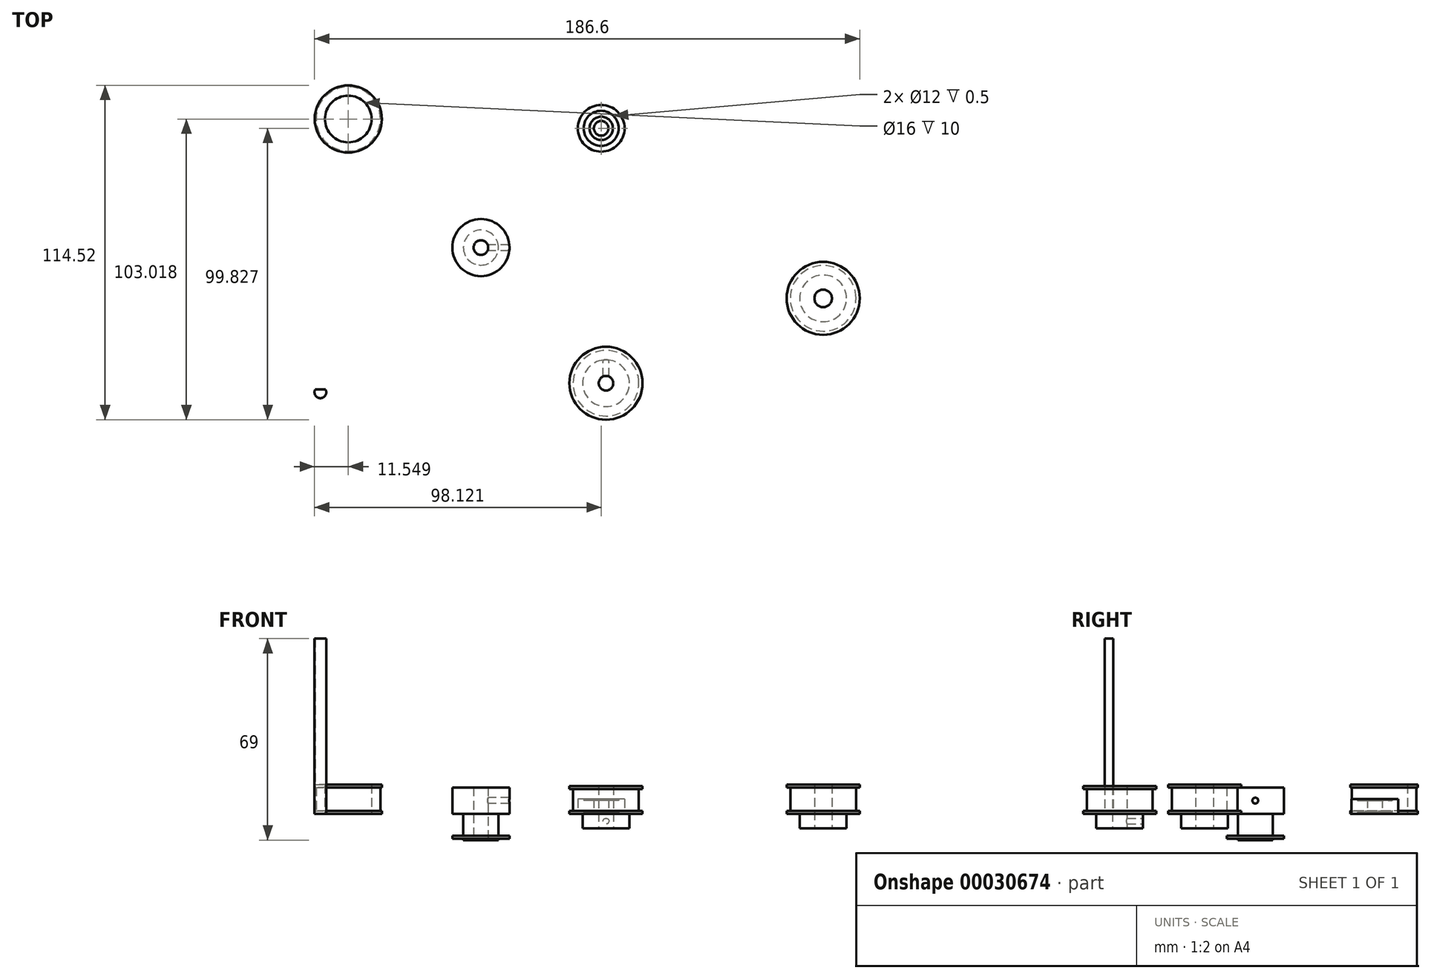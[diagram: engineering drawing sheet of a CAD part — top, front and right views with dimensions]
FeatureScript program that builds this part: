
annotation { "Feature Type Name" : "Feature", "Feature Type Description" : "" }
export const myFeature = defineFeature(function(context is Context, id is Id, definition is map)
    precondition{}
    {
        {
            var Q0;
            Q0=qCreatedBy(makeId("Top.planeOp"),FACE);
            var sketch = newSketch(context, id + "F21", { "sketchPlane" : qUnion([Q0])});
            skCircle(sketch, "E0", {"center": v(0, 0) * mm, "radius": 9.8 * mm});
            skCircle(sketch, "E1", {"center": v(0, 0) * mm, "radius": 6 * mm});
            skSolve(sketch);
        }
        {
            var Q0;
            Q0=makeQuery(id+"F21.imprint","IMPRINT",FACE,{"disambiguationData":[TD([[makeQuery(id+"F21.imprint","IMPRINT",EDGE,{"derivedFrom":sQuery(id+"F21.wireOp",EDGE,"E0")}),1.0]])]});
            var Q1;
            Q1=makeQuery(id+"F21.imprint","IMPRINT",FACE,{"disambiguationData":[TD([[makeQuery(id+"F21.imprint","IMPRINT",EDGE,{"derivedFrom":sQuery(id+"F21.wireOp",EDGE,"E1")}),1.0]])]});
            extrude(context, id + "F0", {"entities" : qUnion([Q0, Q1]), "depth" : 9 * mm});
        }
        {
            var Q0;
            Q0=makeQuery(id+"F21.imprint","IMPRINT",FACE,{"disambiguationData":[TD([[makeQuery(id+"F21.imprint","IMPRINT",EDGE,{"derivedFrom":sQuery(id+"F21.wireOp",EDGE,"E1")}),1.0]])]});
            extrude(context, id + "F1", {"entities" : qUnion([Q0]), "operationType" : NewBodyOperationType.ADD, "oppositeDirection" : true, "depth" : 7.5 * mm});
        }
        {
            var Q0;
            Q0=makeQuery(id+"F1.opExtrude","CAP_FACE",FACE,{"disambiguationData":[OSD([sQuery(id+"F21.wireOp",EDGE,"E1")])],"isStart":false});
            var sketch = newSketch(context, id + "F22", { "sketchPlane" : qUnion([Q0])});
            skCircle(sketch, "E2.0", {"center": v(0, 0) * mm, "radius": 9.8 * mm});
            skCircle(sketch, "E3.0", {"center": v(0, 0) * mm, "radius": 6 * mm});
            skSolve(sketch);
        }
        {
            var Q0;
            Q0 = qSketchRegion(id + "F22", true);
            extrude(context, id + "F2", {"entities" : qUnion([Q0]), "operationType" : NewBodyOperationType.ADD, "depth" : 1 * mm});
        }
        {
            var Q0;
            Q0=makeQuery(id+"F1.opExtrude","CAP_FACE",FACE,{"disambiguationData":[OSD([sQuery(id+"F21.wireOp",EDGE,"E1")])],"isStart":false});
            extrude(context, id + "F23", {"entities" : qUnion([Q0]), "operationType" : NewBodyOperationType.ADD, "depth" : 1.5 * mm});
        }
        {
            var Q0;
            Q0=makeQuery(id+"F23.opExtrude","CAP_FACE",FACE,{"disambiguationData":[OSD([sQuery(id+"F21.wireOp",EDGE,"E1")])],"isStart":false});
            var sketch = newSketch(context, id + "F3", { "sketchPlane" : qUnion([Q0])});
            skPoint(sketch, "E4.0", {"position": v(0, 0) * mm});
            skCircle(sketch, "E5", {"center": v(0, 0) * mm, "radius": 2.5 * mm});
            skSolve(sketch);
        }
        {
            var Q0;
            Q0 = qSketchRegion(id + "F3", true);
            var Q1;
            Q1=makeQuery(id+"F0.opExtrude","CAP_FACE",FACE,{"disambiguationData":[OSD([sQuery(id+"F21.wireOp",EDGE,"E0")])],"isStart":false});
            extrude(context, id + "F4", {"entities" : qUnion([Q0]), "operationType" : NewBodyOperationType.REMOVE, "endBound" : BoundingType.UP_TO_SURFACE, "oppositeDirection" : true, "endBoundEntityFace" : qUnion([Q1]), "depth" : 25 * mm});
        }
        {
            var Q0;
            Q0=qCreatedBy(makeId("Top.planeOp"),FACE);
            var sketch = newSketch(context, id + "F5", { "sketchPlane" : qUnion([Q0])});
            skCircle(sketch, "E6", {"center": v(-45.4, 44.05) * mm, "radius": 11.5 * mm});
            skCircle(sketch, "E7", {"center": v(-45.4, 44.05) * mm, "radius": 11 * mm});
            skCircle(sketch, "E8", {"center": v(-45.4, 44.05) * mm, "radius": 0.1 * mm});
            skCircle(sketch, "E9", {"center": v(-45.4, 44.05) * mm, "radius": 8 * mm});
            skSolve(sketch);
        }
        {
            var Q0;
            Q0=makeQuery(id+"F5.imprint","IMPRINT",FACE,{"disambiguationData":[TD([[makeQuery(id+"F5.imprint","IMPRINT",EDGE,{"derivedFrom":sQuery(id+"F5.wireOp",EDGE,"E7")}),1.0]])]});
            extrude(context, id + "F24", {"entities" : qUnion([Q0]), "depth" : 10 * mm});
        }
        {
            var Q0;
            Q0=makeQuery(id+"F5.imprint","IMPRINT",FACE,{"disambiguationData":[TD([[makeQuery(id+"F5.imprint","IMPRINT",EDGE,{"derivedFrom":sQuery(id+"F5.wireOp",EDGE,"E6")}),1.0]])]});
            extrude(context, id + "F25", {"entities" : qUnion([Q0]), "operationType" : NewBodyOperationType.ADD, "depth" : 1 * mm});
        }
        {
            var Q0;
            Q0=makeQuery(id+"F5.imprint","IMPRINT",FACE,{"disambiguationData":[TD([[makeQuery(id+"F5.imprint","IMPRINT",EDGE,{"derivedFrom":sQuery(id+"F5.wireOp",EDGE,"E6")}),1.0]])]});
            var Q1;
            Q1=makeQuery(id+"F24.opExtrude","CAP_FACE",FACE,{"disambiguationData":[OSD([sQuery(id+"F5.wireOp",EDGE,"E7"),sQuery(id+"F5.wireOp",EDGE,"E9")])],"isStart":false});
            extrude(context, id + "F26", {"entities" : qUnion([Q0]), "operationType" : NewBodyOperationType.ADD, "endBound" : BoundingType.UP_TO_SURFACE, "endBoundEntityFace" : qUnion([Q1]), "depth" : 25 * mm, "hasSecondDirection" : true, "secondDirectionOppositeDirection" : false, "secondDirectionDepth" : 9 * mm});
        }
        {
            var Q0;
            Q0=qCreatedBy(makeId("Top.planeOp"),FACE);
            var sketch = newSketch(context, id + "F6", { "sketchPlane" : qUnion([Q0])});
            skCircle(sketch, "E10", {"center": v(42.82, -46.47) * mm, "radius": 12.5 * mm});
            skCircle(sketch, "E11", {"center": v(42.82, -46.47) * mm, "radius": 11.25 * mm});
            skCircle(sketch, "E12", {"center": v(42.82, -46.47) * mm, "radius": 8 * mm});
            skCircle(sketch, "E13", {"center": v(42.82, -46.47) * mm, "radius": 2.5 * mm});
            skSolve(sketch);
        }
        {
            var Q0;
            Q0=makeQuery(id+"F6.imprint","IMPRINT",FACE,{"disambiguationData":[TD([[makeQuery(id+"F6.imprint","IMPRINT",EDGE,{"derivedFrom":sQuery(id+"F6.wireOp",EDGE,"E11")}),1.0]])]});
            var Q1;
            Q1=makeQuery(id+"F6.imprint","IMPRINT",FACE,{"disambiguationData":[TD([[makeQuery(id+"F6.imprint","IMPRINT",EDGE,{"derivedFrom":sQuery(id+"F6.wireOp",EDGE,"E12")}),1.0]])]});
            extrude(context, id + "F7", {"entities" : qUnion([Q0, Q1]), "depth" : 9.5 * mm});
        }
        {
            var Q0;
            Q0=makeQuery(id+"F6.imprint","IMPRINT",FACE,{"disambiguationData":[TD([[makeQuery(id+"F6.imprint","IMPRINT",EDGE,{"derivedFrom":sQuery(id+"F6.wireOp",EDGE,"E10")}),1.0]])]});
            extrude(context, id + "F27", {"entities" : qUnion([Q0]), "operationType" : NewBodyOperationType.ADD, "depth" : 1 * mm});
        }
        {
            var Q0;
            Q0=makeQuery(id+"F6.imprint","IMPRINT",FACE,{"disambiguationData":[TD([[makeQuery(id+"F6.imprint","IMPRINT",EDGE,{"derivedFrom":sQuery(id+"F6.wireOp",EDGE,"E10")}),1.0]])]});
            extrude(context, id + "F28", {"entities" : qUnion([Q0]), "operationType" : NewBodyOperationType.ADD, "depth" : 9.5 * mm, "hasSecondDirection" : true, "secondDirectionOppositeDirection" : false, "secondDirectionDepth" : 8.5 * mm});
        }
        {
            var Q0;
            Q0=makeQuery(id+"F6.imprint","IMPRINT",FACE,{"disambiguationData":[TD([[makeQuery(id+"F6.imprint","IMPRINT",EDGE,{"derivedFrom":sQuery(id+"F6.wireOp",EDGE,"E12")}),1.0]])]});
            extrude(context, id + "F8", {"entities" : qUnion([Q0]), "operationType" : NewBodyOperationType.ADD, "oppositeDirection" : true, "depth" : 5 * mm});
        }
        {
            var Q0;
            Q0=qCreatedBy(makeId("Front.planeOp"),FACE);
            var sketch = newSketch(context, id + "F9", { "sketchPlane" : qUnion([Q0])});
            skLineSegment(sketch, "E14", {"start": v(50.82, 0) * mm, "end": v(50.82, -5) * mm});
            skLineSegment(sketch, "E15", {"start": v(34.82, -5) * mm, "end": v(34.82, 0) * mm});
            skLineSegment(sketch, "E16.0", {"start": v(30.32, 0) * mm, "end": v(55.32, 0) * mm});
            skLineSegment(sketch, "E17.0", {"start": v(34.82, -5) * mm, "end": v(50.82, -5) * mm});
            skLineSegment(sketch, "E18", {"start": v(34.82, -5) * mm, "end": v(50.82, 0) * mm, "construction": true});
            skCircle(sketch, "E19", {"center": v(42.82, -2.5) * mm, "radius": 1 * mm});
            skSolve(sketch);
        }
        {
            var Q0;
            Q0=makeQuery(id+"F9.imprint","IMPRINT",FACE,{"disambiguationData":[TD([[makeQuery(id+"F9.imprint","IMPRINT",EDGE,{"derivedFrom":sQuery(id+"F9.wireOp",EDGE,"E19")}),1.0]])]});
            extrude(context, id + "F29", {"entities" : qUnion([Q0]), "operationType" : NewBodyOperationType.REMOVE, "depth" : 44.57 * mm});
        }
        {
            var Q0;
            Q0=qCreatedBy(makeId("Right.planeOp"),FACE);
            var sketch = newSketch(context, id + "F10", { "sketchPlane" : qUnion([Q0])});
            skLineSegment(sketch, "E20", {"start": v(-9.8, 0) * mm, "end": v(-9.8, 9) * mm});
            skLineSegment(sketch, "E21", {"start": v(9.8, 9) * mm, "end": v(9.8, 0) * mm});
            skLineSegment(sketch, "E22", {"start": v(9.7, 9.06) * mm, "end": v(-9.8, 0) * mm});
            skCircle(sketch, "E23", {"center": v(-0.04, 4.53) * mm, "radius": 1 * mm});
            skSolve(sketch);
        }
        {
            var Q0;
            {var subQ0=sQuery(id+"F10.wireOp",EDGE,"E23");var subQ1=sQuery(id+"F10.wireOp",EDGE,"E22");var subQ2=makeQuery(id+"F10.imprint","INTERSECT",VERTEX,{"disambiguationData":[OD(0.0)],"derivedFrom":[subQ1,subQ0]});Q0=makeQuery(id+"F10.imprint","IMPRINT",FACE,{"disambiguationData":[TD([[makeQuery(id+"F10.imprint","IMPRINT",EDGE,{"disambiguationData":[TD([[subQ2,1.0]])],"derivedFrom":subQ1}),-1.0]])]});}
            var Q1;
            {var subQ0=sQuery(id+"F10.wireOp",EDGE,"E23");var subQ1=sQuery(id+"F10.wireOp",EDGE,"E22");var subQ2=makeQuery(id+"F10.imprint","INTERSECT",VERTEX,{"disambiguationData":[OD(0.0)],"derivedFrom":[subQ1,subQ0]});Q1=makeQuery(id+"F10.imprint","IMPRINT",FACE,{"disambiguationData":[TD([[makeQuery(id+"F10.imprint","IMPRINT",EDGE,{"disambiguationData":[TD([[subQ2,1.0]])],"derivedFrom":subQ1}),1.0]])]});}
            extrude(context, id + "F11", {"entities" : qUnion([Q0, Q1]), "operationType" : NewBodyOperationType.REMOVE, "depth" : 10.3 * mm});
        }
        {
            var Q0;
            Q0=qCreatedBy(makeId("Top.planeOp"),FACE);
            var sketch = newSketch(context, id + "F12", { "sketchPlane" : qUnion([Q0])});
            skCircle(sketch, "E24", {"center": v(41.17, 40.86) * mm, "radius": 8 * mm});
            skCircle(sketch, "E25", {"center": v(41.17, 40.86) * mm, "radius": 6 * mm});
            skCircle(sketch, "E26", {"center": v(41.17, 40.86) * mm, "radius": 4 * mm});
            skCircle(sketch, "E27", {"center": v(41.17, 40.86) * mm, "radius": 2.5 * mm});
            skSolve(sketch);
        }
        {
            var Q0;
            Q0=makeQuery(id+"F12.imprint","IMPRINT",FACE,{"disambiguationData":[TD([[makeQuery(id+"F12.imprint","IMPRINT",EDGE,{"derivedFrom":sQuery(id+"F12.wireOp",EDGE,"E24")}),1.0]])]});
            var Q1;
            Q1=makeQuery(id+"F12.imprint","IMPRINT",FACE,{"disambiguationData":[TD([[makeQuery(id+"F12.imprint","IMPRINT",EDGE,{"derivedFrom":sQuery(id+"F12.wireOp",EDGE,"E26")}),1.0]])]});
            extrude(context, id + "F30", {"entities" : qUnion([Q0, Q1]), "depth" : 5 * mm});
        }
        {
            var Q0;
            Q0=makeQuery(id+"F12.imprint","IMPRINT",FACE,{"disambiguationData":[TD([[makeQuery(id+"F12.imprint","IMPRINT",EDGE,{"derivedFrom":sQuery(id+"F12.wireOp",EDGE,"E25")}),1.0]])]});
            extrude(context, id + "F13", {"entities" : qUnion([Q0]), "operationType" : NewBodyOperationType.ADD, "depth" : 4.5 * mm, "hasSecondDirection" : true, "secondDirectionOppositeDirection" : false, "secondDirectionDepth" : 0.5 * mm});
        }
        {
            var Q0;
            Q0=qCreatedBy(makeId("Top.planeOp"),FACE);
            var sketch = newSketch(context, id + "F14", { "sketchPlane" : qUnion([Q0])});
            skArc(sketch, "E28", {"start": v(-56.68, -48.6) * mm, "mid": v(-54.95, -51.6) * mm, "end": v(-53.22, -48.6) * mm});
            skLineSegment(sketch, "E29", {"start": v(-56.68, -48.6) * mm, "end": v(-53.22, -48.6) * mm});
            skSolve(sketch);
        }
        {
            var Q0;
            Q0 = qSketchRegion(id + "F14", true);
            extrude(context, id + "F15", {"entities" : qUnion([Q0]), "depth" : 60 * mm});
        }
        {
            var Q0;
            Q0=qCreatedBy(makeId("Top.planeOp"),FACE);
            var sketch = newSketch(context, id + "F16", { "sketchPlane" : qUnion([Q0])});
            skCircle(sketch, "E30", {"center": v(117.15, -17.4) * mm, "radius": 12.5 * mm});
            skCircle(sketch, "E31", {"center": v(117.15, -17.4) * mm, "radius": 11.25 * mm});
            skCircle(sketch, "E32", {"center": v(117.15, -17.4) * mm, "radius": 8 * mm});
            skCircle(sketch, "E33", {"center": v(117.15, -17.4) * mm, "radius": 3 * mm});
            skSolve(sketch);
        }
        {
            var Q0;
            Q0=makeQuery(id+"F16.imprint","IMPRINT",FACE,{"disambiguationData":[TD([[makeQuery(id+"F16.imprint","IMPRINT",EDGE,{"derivedFrom":sQuery(id+"F16.wireOp",EDGE,"E31")}),1.0]])]});
            var Q1;
            Q1=makeQuery(id+"F16.imprint","IMPRINT",FACE,{"disambiguationData":[TD([[makeQuery(id+"F16.imprint","IMPRINT",EDGE,{"derivedFrom":sQuery(id+"F16.wireOp",EDGE,"E32")}),1.0]])]});
            extrude(context, id + "F17", {"entities" : qUnion([Q0, Q1]), "depth" : 10 * mm});
        }
        {
            var Q0;
            Q0=makeQuery(id+"F16.imprint","IMPRINT",FACE,{"disambiguationData":[TD([[makeQuery(id+"F16.imprint","IMPRINT",EDGE,{"derivedFrom":sQuery(id+"F16.wireOp",EDGE,"E32")}),1.0]])]});
            extrude(context, id + "F18", {"entities" : qUnion([Q0]), "operationType" : NewBodyOperationType.ADD, "oppositeDirection" : true, "depth" : 5 * mm});
        }
        {
            var Q0;
            Q0=makeQuery(id+"F16.imprint","IMPRINT",FACE,{"disambiguationData":[TD([[makeQuery(id+"F16.imprint","IMPRINT",EDGE,{"derivedFrom":sQuery(id+"F16.wireOp",EDGE,"E30")}),1.0]])]});
            extrude(context, id + "F19", {"entities" : qUnion([Q0]), "operationType" : NewBodyOperationType.ADD, "depth" : 1 * mm});
        }
        {
            var Q0;
            Q0=makeQuery(id+"F16.imprint","IMPRINT",FACE,{"disambiguationData":[TD([[makeQuery(id+"F16.imprint","IMPRINT",EDGE,{"derivedFrom":sQuery(id+"F16.wireOp",EDGE,"E30")}),1.0]])]});
            var Q1;
            Q1=makeQuery(id+"F17.opExtrude","CAP_FACE",FACE,{"disambiguationData":[OSD([sQuery(id+"F16.wireOp",EDGE,"E31"),sQuery(id+"F16.wireOp",EDGE,"E33")])],"isStart":false});
            extrude(context, id + "F20", {"entities" : qUnion([Q0]), "operationType" : NewBodyOperationType.ADD, "endBound" : BoundingType.UP_TO_SURFACE, "endBoundEntityFace" : qUnion([Q1]), "depth" : 25 * mm, "hasSecondDirection" : true, "secondDirectionOppositeDirection" : false, "secondDirectionDepth" : 9 * mm});
        }
    });
